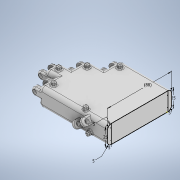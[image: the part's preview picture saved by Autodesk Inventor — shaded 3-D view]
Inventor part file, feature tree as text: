
AUTODESK INVENTOR PART (.ipt)
format: ipt  version: 2022 (Build 260153000, 153)  size: 1,103,872 bytes
history: native  units: mm
features: sketch x27, extrude x26, fillet x8, other x6
ambient origin geometry x8: Origin, YZ Plane, XZ Plane, XY Plane, X Axis, Y Axis, Z Axis, Center Point
bodies: Solide1 (feature_tree)
feature tree (67):
  extrude  "Extrusion1"  Depth=110.0mm
  other  "Plan de construction3"
  extrude  "Extrusion9"  Depth=88.0mm
  extrude  "Extrusion10"  Depth=25.0mm TaperAngle=0.0deg
  extrude  "Extrusion11"  Depth=25.0mm
  extrude  "Extrusion13"  Depth=22.0mm
  extrude  "Extrusion14"  Depth=22.0mm
  sketch  "Esquisse30"
  sketch  "Esquisse31"
  sketch  "Esquisse32"
  sketch  "Esquisse33"
  extrude  "Extrusion25"  Depth=22.0mm
  extrude  "Extrusion26"  Depth=22.0mm
  extrude  "Extrusion27"  Depth=2.0mm
  extrude  "Extrusion28"  Depth=2.0mm
  sketch  "Esquisse34"
  sketch  "Esquisse35"
  sketch  "Esquisse36"
  sketch  "Esquisse37"
  extrude  "Extrusion29"  Depth=2.0mm
  extrude  "Extrusion30"  Depth=20.0mm
  extrude  "Extrusion31"  Depth=6.0mm
  extrude  "Extrusion32"  Depth=8.0mm
  extrude  "Extrusion33"  Depth=5.0mm
  extrude  "Extrusion34"  Depth=5.0mm
  extrude  "Extrusion35"  Depth=10.0mm TaperAngle=0.0deg
  extrude  "Extrusion36"  Depth=5.0mm
  extrude  "Extrusion37"  Depth=20.0mm TaperAngle=0.0deg
  extrude  "Extrusion38"  Depth=15.0mm TaperAngle=0.0deg
  extrude  "Extrusion39"  Depth=17.0mm TaperAngle=0.0deg
  extrude  "Extrusion40"  Depth=40.0mm TaperAngle=0.0deg
  other  "Révolution1"
  fillet  "Congé14"  Radius=20.0mm
  fillet  "Congé15"  Radius=6.0mm
  fillet  "Congé16"  Radius=7.0mm
  fillet  "Congé17"  Radius=5.0mm
  fillet  "Congé18"  Radius=6.0mm
  fillet  "Congé20"  Radius=10.0mm
  fillet  "Congé21"  Radius=20.0mm
  extrude  "Extrusion41"  Depth=5.0mm
  other  "Révolution3"
  extrude  "Extrusion42"  Depth=10.0mm
  extrude  "Extrusion43"  Depth=5.0mm
  extrude  "Extrusion44"  Depth=5.0mm
  other  "Révolution4"
  other  "Révolution5"
  other  "Révolution6"
  fillet  "Congé22"  Radius=10.0mm
  sketch  "Esquisse57"
  sketch  "Esquisse18"
  sketch  "Esquisse38"
  sketch  "Esquisse40"
  sketch  "Esquisse41"
  sketch  "Esquisse42"
  sketch  "Esquisse43"
  sketch  "Esquisse44"
  sketch  "Esquisse45"
  sketch  "Esquisse46"
  sketch  "Esquisse47"
  sketch  "Esquisse48"
  sketch  "Esquisse50"
  sketch  "Esquisse51"
  sketch  "Esquisse52"
  sketch  "Esquisse53"
  sketch  "Esquisse54"
  sketch  "Esquisse55"
  sketch  "Esquisse56"
